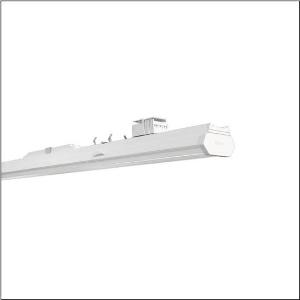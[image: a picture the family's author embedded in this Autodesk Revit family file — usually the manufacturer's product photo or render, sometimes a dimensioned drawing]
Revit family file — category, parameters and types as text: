
# Revit family: licross_r__11_protected_mo_51td1bdn68xg3s_e11a
name_source: partatom
category: Lighting Fixtures
units: mm (PartAtom-declared; Revit-internal decimal feet)

## family parameters
Cut with Voids When Loaded = No
Host = Face
Light Source = No
Part Type = Normal
Room Calculation Point = No
Round Connector Dimension = Use Diameter
Shared = No

## types (1)
- --- (1 x LED, 900 lm, 6.8 W, 6500K)
    Apparent Load = 7 VA
    CIE Flux Codes = 54 82 95 97 100
    Color Rendering = 80
    Color Temperature = 6500K
    Default Elevation = 1800 mm
    Description = Licross® 11 Protected MO, luminaire insert, of sheet steel, galvanised, coil coated, white, length: 1.500mm, width: 90mm, height: 101mm, LED rated luminous flux: 8.310lm, light colour: 865, SDCM (Standard Deviation of Colour Matching)MacAdam ≤ 2 SDCM (initial), control gear: DALI 2 (for two DALI lines), with plug, 6-pole, with phase selection, for trunking rail, 14-core, mains connection: 220..240V, AC, 50/60Hz, rated input power: 55W, for trunking rail, 14-core, internal wiring halogen-free, for emergency light function, converter,control gear: single battery element, battery: LiFePO4, 9Ah, primary optical cover: cover, of PMMA, light emission: direct distribution, primary light characteristic: symmetric, protection rating (complete): IP54, insulation class (complete): insulation class I (protective earthing), certification: CE, UKCA, protection symbol: D if used in an environment with non-conductive dust loads with corresponding accessories, impact resistance: IK06, permissible ambient temperature for indoor applications: +5..+35°C, standard: EN 60598-2-22, corresponds to IFS (International Featured Standards) requirements for safety and quality in the food industry, reducing of maximum allowable ambient temperature of 5°C with ceiling mounting, LABS conformity tested according to VDMA 24364:2018-05, packaging unit: 1 piece
    Height = 92 mm
    Lamp = 1 x LED
    Lamp Light Flux = 900 lm
    Lamp Power = 6.8 W
    Lamp count = 1
    Length = 1500 mm
    Luminous efficacy = 132 lm/W
    Manufacturer = Siteco
    ModVariant = No
    Model = 51TD1BDN68XG3S
    Mounting Place = Ceiling
    Mounting Type = Pendant
    Number of Poles = 1
    OnlyDefault = Yes
    Power Factor = 1
    Product Name = Licross® 11 Protected MO
    Product group = luminaire insert | ceiling pendant
    ProductGroupID = 901
    Protection Class = Protection class I
    Protection Degree = IP 54
    RLX_Detail_Level = 1
    RLX_Emergency_Light_Flux = 0 lm
    RLX_Emergency_Type = 0
    RLX_Emergency_Type_DB = No
    RlxData = <blob elided: 24885 chars, md5=0f78c5ce>
    Socket = socket
    Standby Power = 0 W
    System Light Flux = 900 lm
    System Power = 7 W
    Type Comments = : emergency light operation: 3 h
    Type Image = l_1256145.jpg
    URL = http://relux.com
    VarID = @adj_040365
    Voltage = 0 V
    Weight = 0.00 kg
    Width = 88 mm

## geometry (parser evidence)
native form markers: Blend x4, Sweep x9
no freeform markers — native parametric forms only
